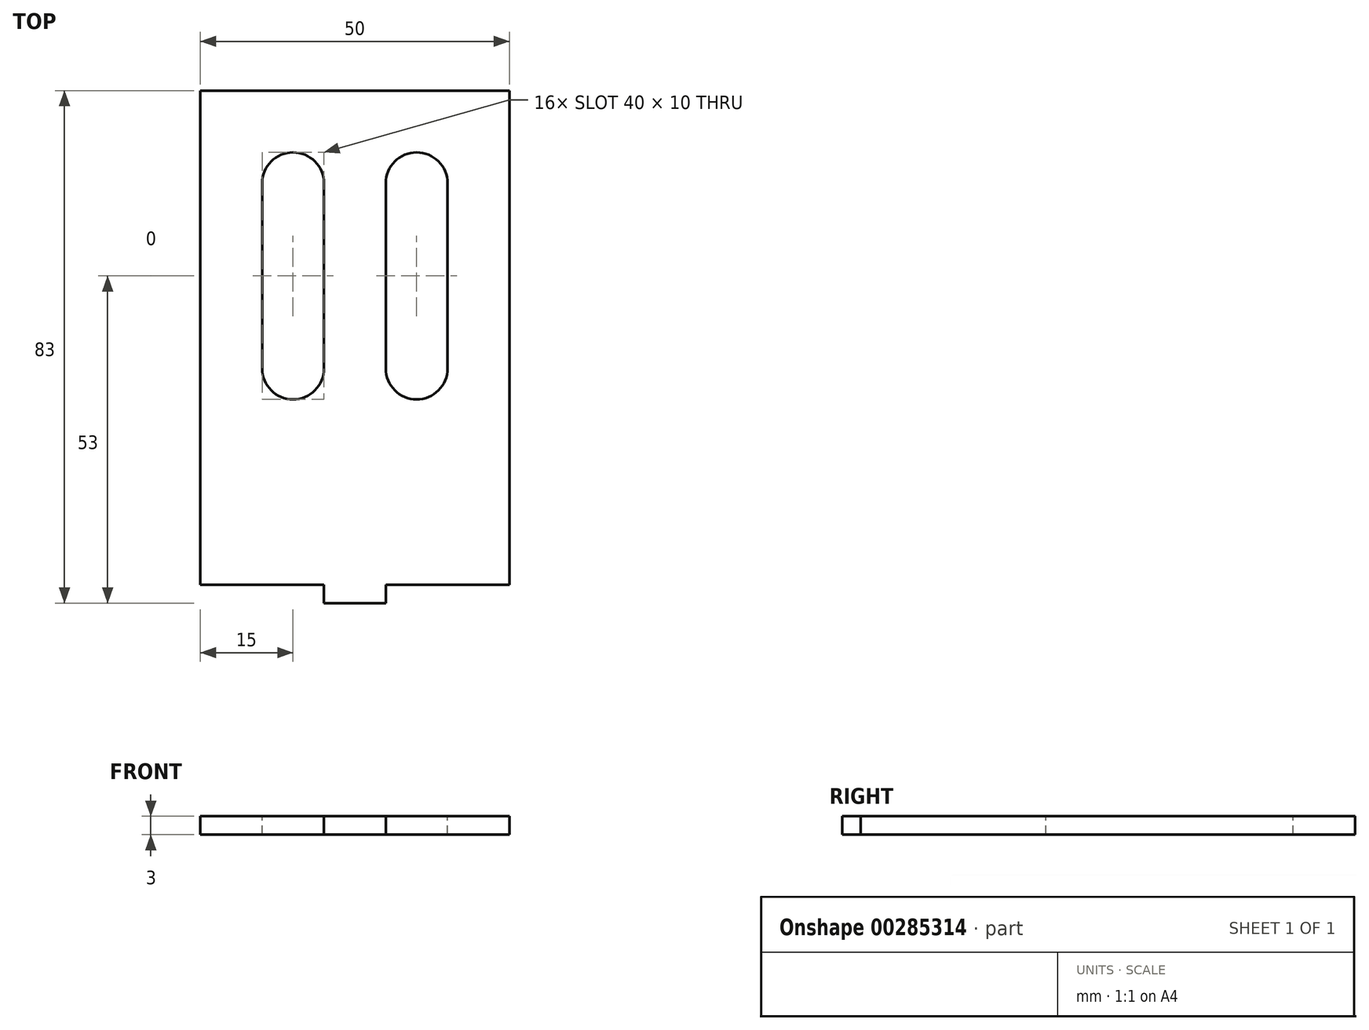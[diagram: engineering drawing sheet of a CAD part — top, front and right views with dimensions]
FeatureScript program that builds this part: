
annotation { "Feature Type Name" : "Feature", "Feature Type Description" : "" }
export const myFeature = defineFeature(function(context is Context, id is Id, definition is map)
    precondition{}
    {
        {
            var Q0;
            Q0=qCreatedBy(makeId("Top.planeOp"),FACE);
            var sketch = newSketch(context, id + "F0", { "sketchPlane" : qUnion([Q0])});
            skLineSegment(sketch, "E0.top", {"start": v(25, 40) * mm, "end": v(-25, 40) * mm});
            skLineSegment(sketch, "E0.left", {"start": v(25, -40) * mm, "end": v(25, 40) * mm});
            skLineSegment(sketch, "E0.right", {"start": v(-25, -40) * mm, "end": v(-25, 40) * mm});
            skPoint(sketch, "E0.middle", {"position": v(0, 0) * mm});
            skLineSegment(sketch, "E1", {"start": v(-25, -40) * mm, "end": v(-5, -40) * mm});
            skLineSegment(sketch, "E2", {"start": v(-5, -40) * mm, "end": v(-5, -43) * mm});
            skLineSegment(sketch, "E3", {"start": v(-5, -43) * mm, "end": v(5, -43) * mm});
            skLineSegment(sketch, "E4", {"start": v(5, -43) * mm, "end": v(5, -40) * mm});
            skLineSegment(sketch, "E5", {"start": v(5, -40) * mm, "end": v(25, -40) * mm});
            skPoint(sketch, "E6", {"position": v(0, -43) * mm});
            skSolve(sketch);
        }
        {
            var Q0;
            Q0 = qSketchRegion(id + "F0", true);
            extrude(context, id + "F1", {"entities" : qUnion([Q0]), "depth" : 3 * mm});
        }
        {
            var Q0;
            Q0=makeQuery(id+"F1.opExtrude","CAP_FACE",FACE,{"disambiguationData":[OSD([sQuery(id+"F0.wireOp",EDGE,"E0.top"),sQuery(id+"F0.wireOp",EDGE,"E0.left"),sQuery(id+"F0.wireOp",EDGE,"E0.right"),sQuery(id+"F0.wireOp",EDGE,"E1"),sQuery(id+"F0.wireOp",EDGE,"E2"),sQuery(id+"F0.wireOp",EDGE,"E3"),sQuery(id+"F0.wireOp",EDGE,"E4"),sQuery(id+"F0.wireOp",EDGE,"E5")])],"isStart":false});
            var sketch = newSketch(context, id + "F2", { "sketchPlane" : qUnion([Q0])});
            skLineSegment(sketch, "E7", {"start": v(-10, 25) * mm, "end": v(-10, -5) * mm});
            skLineSegment(sketch, "E8", {"start": v(10, 25) * mm, "end": v(10, -5) * mm});
            skLineSegment(sketch, "E9", {"start": v(-10, 25) * mm, "end": v(10, 25) * mm, "construction": true});
            skLineSegment(sketch, "E10", {"start": v(10, -5) * mm, "end": v(-10, -5) * mm, "construction": true});
            skPoint(sketch, "E11", {"position": v(0, 25) * mm});
            skArc(sketch, "E12.0.startCap", {"start": v(-15, 25) * mm, "mid": v(-10, 30) * mm, "end": v(-5, 25) * mm});
            skArc(sketch, "E12.0.endCap", {"start": v(-5, -5) * mm, "mid": v(-10, -10) * mm, "end": v(-15, -5) * mm});
            skLineSegment(sketch, "E12.0.left", {"start": v(-5, 25) * mm, "end": v(-5, -5) * mm});
            skLineSegment(sketch, "E12.0.right", {"start": v(-15, 25) * mm, "end": v(-15, -5) * mm});
            skArc(sketch, "E12.1.startCap", {"start": v(5, 25) * mm, "mid": v(10, 30) * mm, "end": v(15, 25) * mm});
            skArc(sketch, "E12.1.endCap", {"start": v(15, -5) * mm, "mid": v(10, -10) * mm, "end": v(5, -5) * mm});
            skLineSegment(sketch, "E12.1.left", {"start": v(15, 25) * mm, "end": v(15, -5) * mm});
            skLineSegment(sketch, "E12.1.right", {"start": v(5, 25) * mm, "end": v(5, -5) * mm});
            skSolve(sketch);
        }
        {
            var Q0;
            Q0 = qSketchRegion(id + "F2", true);
            extrude(context, id + "F3", {"entities" : qUnion([Q0]), "operationType" : NewBodyOperationType.REMOVE, "endBound" : BoundingType.UP_TO_NEXT, "oppositeDirection" : true, "depth" : 25 * mm});
        }
    });
